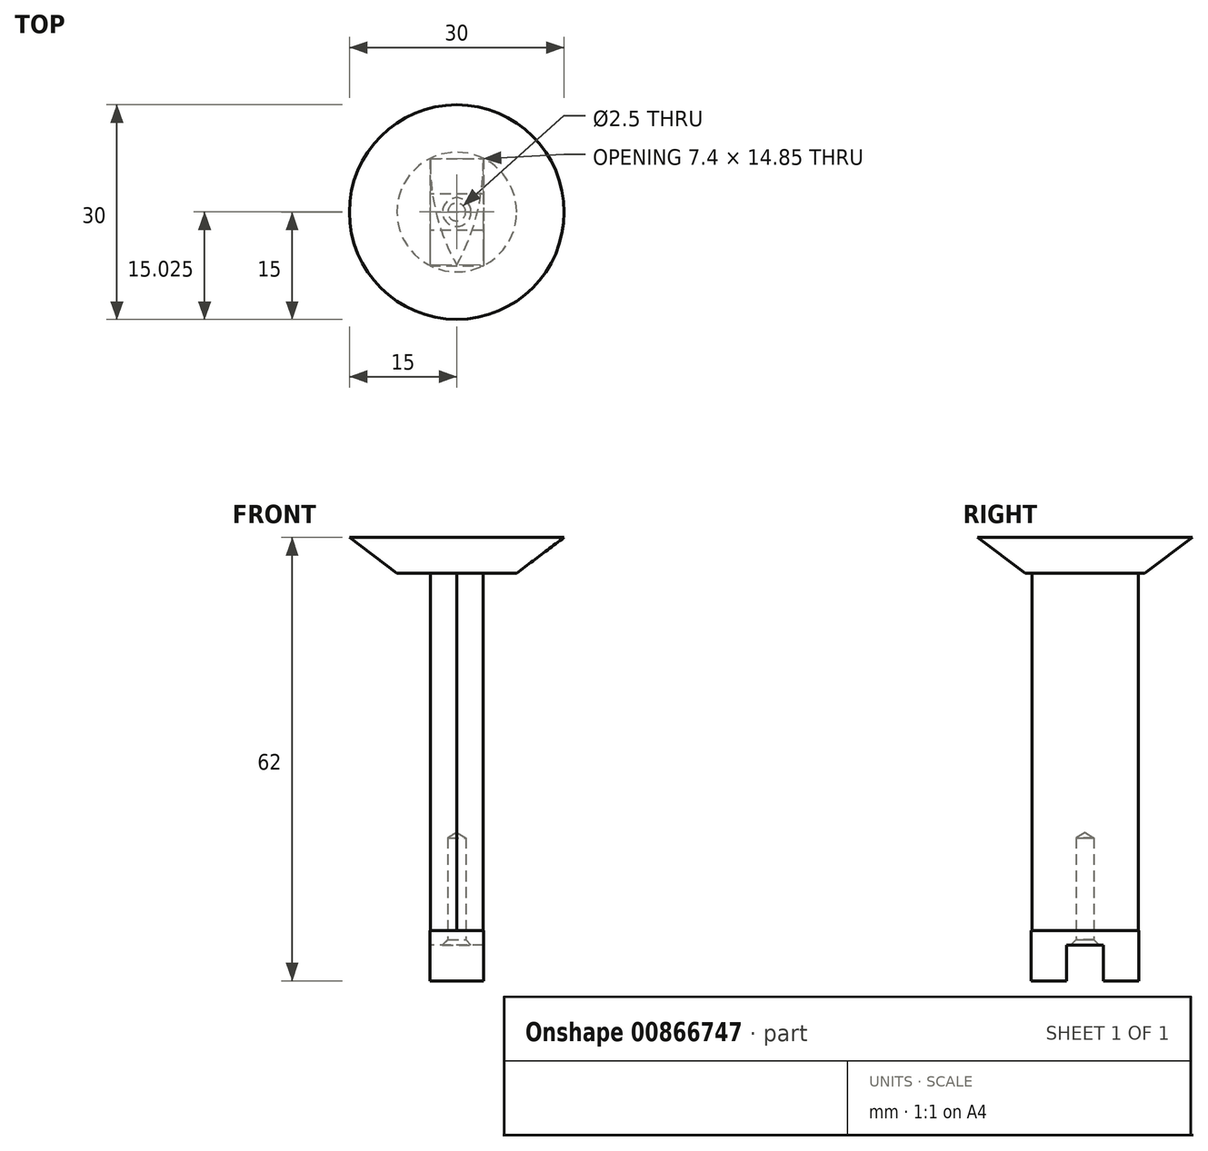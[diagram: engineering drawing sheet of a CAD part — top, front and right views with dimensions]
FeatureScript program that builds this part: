
annotation { "Feature Type Name" : "Feature", "Feature Type Description" : "" }
export const myFeature = defineFeature(function(context is Context, id is Id, definition is map)
    precondition{}
    {
        {
            var Q0;
            Q0=qCreatedBy(makeId("Top.planeOp"),FACE);
            var sketch = newSketch(context, id + "F0", { "sketchPlane" : qUnion([Q0])});
            skLineSegment(sketch, "E0.bottom", {"start": v(-3.75, 7.5) * mm, "end": v(3.75, 7.5) * mm});
            skLineSegment(sketch, "E0.top", {"start": v(-3.75, -7.5) * mm, "end": v(3.75, -7.5) * mm});
            skLineSegment(sketch, "E0.left", {"start": v(-3.75, 7.5) * mm, "end": v(-3.75, -7.5) * mm});
            skLineSegment(sketch, "E0.right", {"start": v(3.75, 7.5) * mm, "end": v(3.75, -7.5) * mm});
            skPoint(sketch, "E0.middle", {"position": v(0, 0) * mm});
            skSolve(sketch);
        }
        {
            var Q0;
            Q0=makeQuery(id+"F0.imprint","IMPRINT",FACE,{"disambiguationData":[TD([[makeQuery(id+"F0.imprint","IMPRINT",EDGE,{"derivedFrom":sQuery(id+"F0.wireOp",EDGE,"E0.bottom")}),-1.0]])]});
            extrude(context, id + "F1", {"entities" : qUnion([Q0]), "depth" : 7 * mm, "offsetDistance" : 25 * mm});
        }
        {
            var Q0;
            Q0=makeQuery(id+"F1.opExtrude","CAP_FACE",FACE,{"disambiguationData":[OSD([sQuery(id+"F0.wireOp",EDGE,"E0.bottom"),sQuery(id+"F0.wireOp",EDGE,"E0.top"),sQuery(id+"F0.wireOp",EDGE,"E0.left"),sQuery(id+"F0.wireOp",EDGE,"E0.right")])],"isStart":true});
            var sketch = newSketch(context, id + "F2", { "sketchPlane" : qUnion([Q0])});
            skLineSegment(sketch, "E1.bottom", {"start": v(3.75, -2.55) * mm, "end": v(-3.75, -2.55) * mm});
            skLineSegment(sketch, "E1.top", {"start": v(3.75, 2.55) * mm, "end": v(-3.75, 2.55) * mm});
            skLineSegment(sketch, "E1.left", {"start": v(3.75, -2.55) * mm, "end": v(3.75, 2.55) * mm});
            skLineSegment(sketch, "E1.right", {"start": v(-3.75, -2.55) * mm, "end": v(-3.75, 2.55) * mm});
            skPoint(sketch, "E1.middle", {"position": v(0, 0) * mm});
            skSolve(sketch);
        }
        {
            var Q0;
            Q0=makeQuery(id+"F2.imprint","IMPRINT",FACE,{"disambiguationData":[TD([[makeQuery(id+"F2.imprint","IMPRINT",EDGE,{"derivedFrom":sQuery(id+"F2.wireOp",EDGE,"E1.bottom")}),-1.0]])]});
            extrude(context, id + "F3", {"entities" : qUnion([Q0]), "operationType" : NewBodyOperationType.REMOVE, "oppositeDirection" : true, "depth" : 5 * mm, "offsetDistance" : 25 * mm});
        }
        {
            var Q0;
            Q0=makeQuery(id+"F1.opExtrude","CAP_FACE",FACE,{"disambiguationData":[OSD([sQuery(id+"F0.wireOp",EDGE,"E0.bottom"),sQuery(id+"F0.wireOp",EDGE,"E0.top"),sQuery(id+"F0.wireOp",EDGE,"E0.left"),sQuery(id+"F0.wireOp",EDGE,"E0.right")])],"isStart":false});
            var sketch = newSketch(context, id + "F4", { "sketchPlane" : qUnion([Q0])});
            skLineSegment(sketch, "E2.bottom", {"start": v(-3.7, 7.45) * mm, "end": v(3.7, 7.45) * mm});
            skLineSegment(sketch, "E2.top", {"start": v(-3.7, -7.45) * mm, "end": v(3.7, -7.45) * mm});
            skLineSegment(sketch, "E2.left", {"start": v(-3.7, 7.45) * mm, "end": v(-3.7, -7.45) * mm});
            skLineSegment(sketch, "E2.right", {"start": v(3.7, 7.45) * mm, "end": v(3.7, -7.45) * mm});
            skPoint(sketch, "E2.middle", {"position": v(0, 0) * mm});
            skSolve(sketch);
        }
        {
            var Q0;
            Q0=makeQuery(id+"F4.imprint","IMPRINT",FACE,{"disambiguationData":[TD([[makeQuery(id+"F4.imprint","IMPRINT",EDGE,{"derivedFrom":sQuery(id+"F4.wireOp",EDGE,"E2.bottom")}),-1.0]])]});
            extrude(context, id + "F5", {"entities" : qUnion([Q0]), "operationType" : NewBodyOperationType.ADD, "depth" : 50 * mm, "offsetDistance" : 25 * mm});
        }
        {
            var Q0;
            Q0=makeQuery(id+"F5.opExtrude","CAP_FACE",FACE,{"disambiguationData":[OSD([sQuery(id+"F4.wireOp",EDGE,"E2.bottom"),sQuery(id+"F4.wireOp",EDGE,"E2.top"),sQuery(id+"F4.wireOp",EDGE,"E2.left"),sQuery(id+"F4.wireOp",EDGE,"E2.right")])],"isStart":false});
            var sketch = newSketch(context, id + "F6", { "sketchPlane" : qUnion([Q0])});
            skCircle(sketch, "E3", {"center": v(0, 0) * mm, "radius": 15 * mm});
            skSolve(sketch);
        }
        {
            var Q0;
            Q0=makeQuery(id+"F6.imprint","IMPRINT",FACE,{"disambiguationData":[TD([[makeQuery(id+"F6.imprint","IMPRINT",EDGE,{"derivedFrom":sQuery(id+"F6.wireOp",EDGE,"E3")}),1.0]])]});
            var Q1;
            Q1=makeQuery(id+"F6.imprint","IMPRINT",FACE,{"disambiguationData":[TD([[makeQuery(id+"F6.imprint","IMPRINT",EDGE,{"derivedFrom":makeQuery(id+"F5.opExtrude","CAP_EDGE",EDGE,{"disambiguationData":[OSD([sQuery(id+"F4.wireOp",EDGE,"E2.bottom")])],"isStart":false})}),-1.0]])]});
            extrude(context, id + "F7", {"entities" : qUnion([Q0, Q1]), "operationType" : NewBodyOperationType.ADD, "depth" : 5 * mm, "offsetDistance" : 25 * mm});
        }
        {
            var Q0;
            Q0=makeQuery(id+"F7.opExtrude","CAP_EDGE",EDGE,{"disambiguationData":[OSD([sQuery(id+"F6.wireOp",EDGE,"E3")])],"isStart":true});
            chamfer(context, id + "F8", {"entities" : qUnion([Q0]), "chamferType" : ChamferType.OFFSET_ANGLE, "width" : 5 * mm, "oppositeDirection" : false, "angle" : 53 * degree, "tangentPropagation" : true});
        }
        {
            var Q0;
            Q0=makeQuery(id+"F5.opExtrude","SWEPT_EDGE",EDGE,{"disambiguationData":[OSD([sQuery(id+"F4.wireOp",EDGE,"E2.top"),sQuery(id+"F4.wireOp",EDGE,"E2.left")])]});
            var Q1;
            Q1=makeQuery(id+"F5.opExtrude","SWEPT_EDGE",EDGE,{"disambiguationData":[OSD([sQuery(id+"F4.wireOp",EDGE,"E2.top"),sQuery(id+"F4.wireOp",EDGE,"E2.right")])]});
            chamfer(context, id + "F9", {"entities" : qUnion([Q0, Q1]), "width" : 3.75 * mm, "tangentPropagation" : true});
        }
        {
            var Q0;
            {var subQ0=sQuery(id+"F4.wireOp",EDGE,"E2.left");Q0=makeQuery(id+"F9.opChamfer","BLEND_EDGE",EDGE,{"blendedFrom":[makeQuery(id+"F5.opExtrude","SWEPT_EDGE",EDGE,{"disambiguationData":[OSD([sQuery(id+"F4.wireOp",EDGE,"E2.top"),subQ0])]}),makeQuery(id+"F5.opExtrude","SWEPT_FACE",FACE,{"disambiguationData":[OSD([subQ0])]})],"blendedInto":[makeQuery(id+"F5.opExtrude","SWEPT_FACE",FACE,{"disambiguationData":[OSD([subQ0])]})]});}
            var Q1;
            {var subQ0=sQuery(id+"F4.wireOp",EDGE,"E2.right");Q1=makeQuery(id+"F9.opChamfer","BLEND_EDGE",EDGE,{"blendedFrom":[makeQuery(id+"F5.opExtrude","SWEPT_EDGE",EDGE,{"disambiguationData":[OSD([sQuery(id+"F4.wireOp",EDGE,"E2.top"),subQ0])]}),makeQuery(id+"F5.opExtrude","SWEPT_FACE",FACE,{"disambiguationData":[OSD([subQ0])]})],"blendedInto":[makeQuery(id+"F5.opExtrude","SWEPT_FACE",FACE,{"disambiguationData":[OSD([subQ0])]})]});}
            fillet(context, id + "F10", {"entities" : qUnion([Q0, Q1]), "radius" : 29.13 * mm, "tangentPropagation" : true, "allowEdgeOverflow" : false});
        }
        {
            var Q0;
            Q0=makeQuery(id+"F3.boolean.opBoolean","COPY",FACE,{"derivedFrom":makeQuery(id+"F3.opExtrude","CAP_FACE",FACE,{"disambiguationData":[OSD([sQuery(id+"F2.wireOp",EDGE,"E1.bottom"),sQuery(id+"F2.wireOp",EDGE,"E1.top"),sQuery(id+"F2.wireOp",EDGE,"E1.left"),sQuery(id+"F2.wireOp",EDGE,"E1.right")])],"isStart":false})});
            var sketch = newSketch(context, id + "F11", { "sketchPlane" : qUnion([Q0])});
            skPoint(sketch, "E4", {"position": v(0, 0) * mm});
            skSolve(sketch);
        }
        {
            var Q0;
            Q0=sQuery(id+"F11.wireOp",VERTEX,"E4");
            var Q1;
            Q1=makeQuery(id+"F1.opExtrude","SWEPT_BODY",BODY,{"disambiguationData":[OSD([sQuery(id+"F0.wireOp",EDGE,"E0.bottom"),sQuery(id+"F0.wireOp",EDGE,"E0.top"),sQuery(id+"F0.wireOp",EDGE,"E0.left"),sQuery(id+"F0.wireOp",EDGE,"E0.right")])]});
            hole(context, id + "F12", {"style" : HoleStyle.C_SINK, "endStyle" : HoleEndStyle.BLIND, "holeDiameter" : 2.5 * mm, "cSinkDiameter" : 4 * mm, "cSinkAngle" : 90 * degree, "majorDiameter" : 5 * mm, "holeDepth" : 15 * mm, "isTappedThrough" : true, "tappedDepth" : 12 * mm, "tapClearance" : 3, "startFromSketch" : true, "locations" : qUnion([Q0]), "scope" : qUnion([Q1])});
        }
    });
